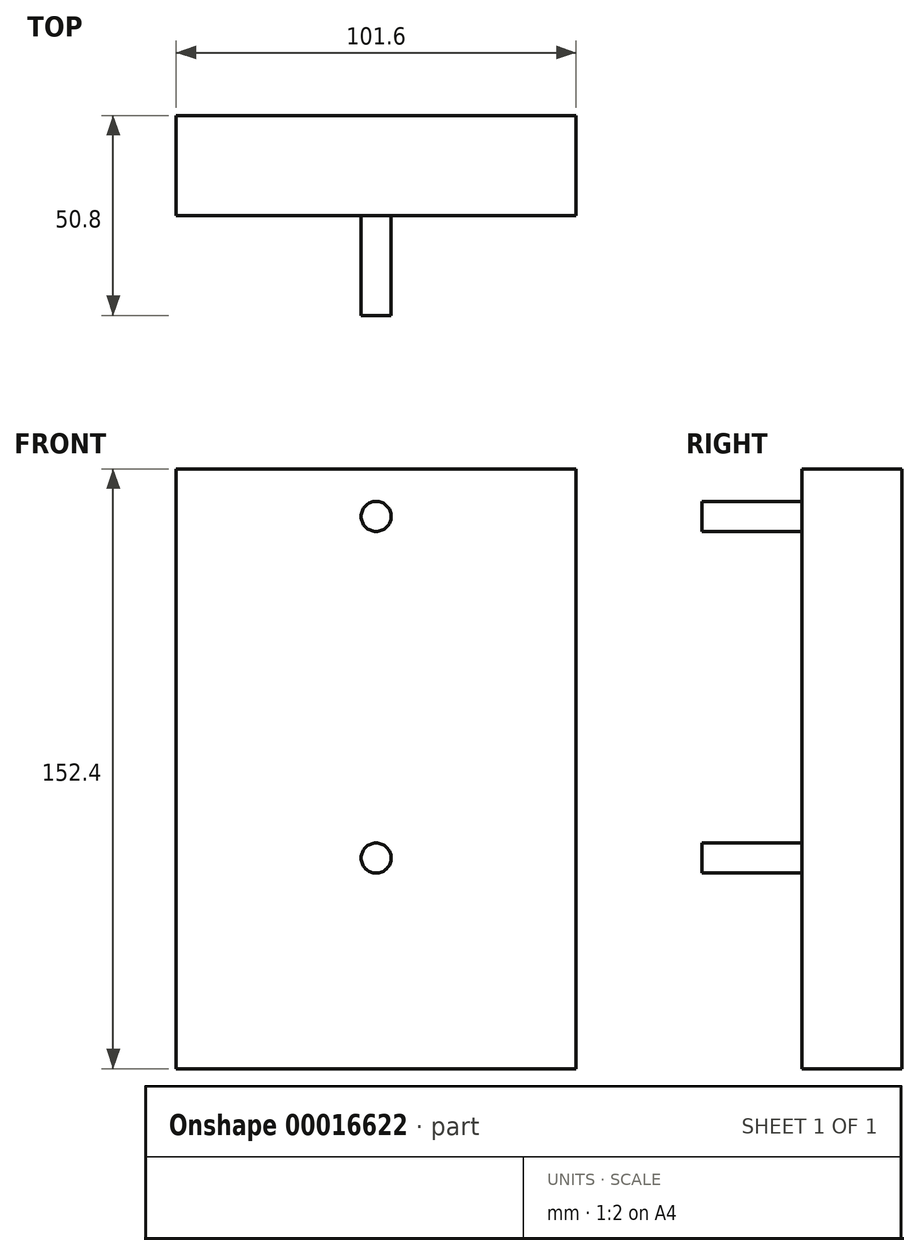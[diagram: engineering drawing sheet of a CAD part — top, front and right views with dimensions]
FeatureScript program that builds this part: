
annotation { "Feature Type Name" : "Feature", "Feature Type Description" : "" }
export const myFeature = defineFeature(function(context is Context, id is Id, definition is map)
    precondition{}
    {
        {
            var Q0;
            Q0=qCreatedBy(makeId("Front.planeOp"),FACE);
            var sketch = newSketch(context, id + "F0", { "sketchPlane" : qUnion([Q0])});
            skLineSegment(sketch, "E0.rect.bottom", {"start": v(-50.8, 76.2) * mm, "end": v(50.8, 76.2) * mm});
            skLineSegment(sketch, "E0.rect.top", {"start": v(-50.8, -76.2) * mm, "end": v(50.8, -76.2) * mm});
            skLineSegment(sketch, "E0.rect.left", {"start": v(-50.8, 76.2) * mm, "end": v(-50.8, -76.2) * mm});
            skLineSegment(sketch, "E0.rect.right", {"start": v(50.8, 76.2) * mm, "end": v(50.8, -76.2) * mm});
            skPoint(sketch, "E0.rect.middle", {"position": v(0, 0) * mm});
            skSolve(sketch);
        }
        {
            var Q0;
            Q0 = qSketchRegion(id + "F0", true);
            extrude(context, id + "F1", {"entities" : qUnion([Q0]), "depth" : 25.4 * mm});
        }
        {
            var Q0;
            Q0=makeQuery(id+"F1.opExtrude","CAP_FACE",FACE,{"disambiguationData":[OSD([sQuery(id+"F0.wireOp",EDGE,"E0.rect.bottom"),sQuery(id+"F0.wireOp",EDGE,"E0.rect.top"),sQuery(id+"F0.wireOp",EDGE,"E0.rect.left"),sQuery(id+"F0.wireOp",EDGE,"E0.rect.right")])],"isStart":false});
            var sketch = newSketch(context, id + "F2", { "sketchPlane" : qUnion([Q0])});
            skCircle(sketch, "E1", {"center": v(0, 64.11) * mm, "radius": 3.81 * mm});
            skCircle(sketch, "E2", {"center": v(0, -22.7) * mm, "radius": 3.81 * mm});
            skSolve(sketch);
        }
        {
            var Q0;
            Q0=makeQuery(id+"F2.imprint","IMPRINT",FACE,{"disambiguationData":[TD([[makeQuery(id+"F2.imprint","IMPRINT",EDGE,{"derivedFrom":sQuery(id+"F2.wireOp",EDGE,"E2")}),1.0]])]});
            var Q1;
            Q1=makeQuery(id+"F2.imprint","IMPRINT",FACE,{"disambiguationData":[TD([[makeQuery(id+"F2.imprint","IMPRINT",EDGE,{"derivedFrom":sQuery(id+"F2.wireOp",EDGE,"E1")}),1.0]])]});
            extrude(context, id + "F3", {"entities" : qUnion([Q0, Q1]), "operationType" : NewBodyOperationType.ADD, "depth" : 25.4 * mm});
        }
    });
